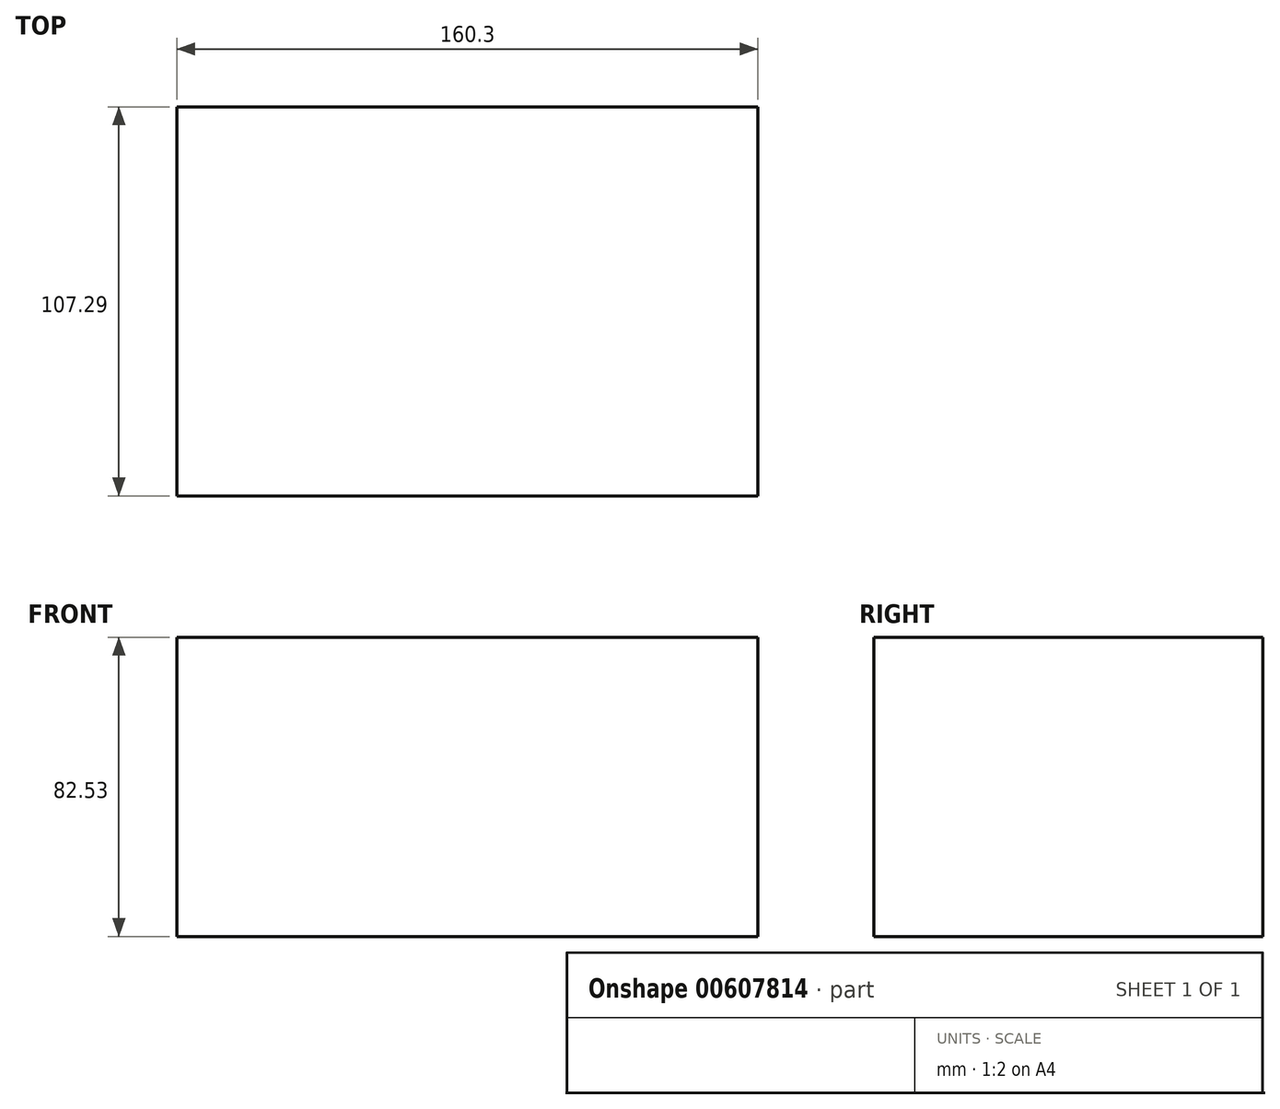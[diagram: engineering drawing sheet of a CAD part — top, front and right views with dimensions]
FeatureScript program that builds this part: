
annotation { "Feature Type Name" : "Feature", "Feature Type Description" : "" }
export const myFeature = defineFeature(function(context is Context, id is Id, definition is map)
    precondition{}
    {
        {
            var Q0;
            Q0=qCreatedBy(makeId("Top.planeOp"),FACE);
            var sketch = newSketch(context, id + "F0", { "sketchPlane" : qUnion([Q0])});
            skLineSegment(sketch, "E0.bottom", {"start": v(76.05, -45.67) * mm, "end": v(-84.25, -45.67) * mm});
            skLineSegment(sketch, "E0.top", {"start": v(76.05, 61.62) * mm, "end": v(-84.25, 61.62) * mm});
            skLineSegment(sketch, "E0.left", {"start": v(76.05, -45.67) * mm, "end": v(76.05, 61.62) * mm});
            skLineSegment(sketch, "E0.right", {"start": v(-84.25, -45.67) * mm, "end": v(-84.25, 61.62) * mm});
            skSolve(sketch);
        }
        {
            var Q0;
            Q0 = qSketchRegion(id + "F0", true);
            extrude(context, id + "F1", {"entities" : qUnion([Q0]), "depth" : 82.53 * mm, "offsetDistance" : 25.4 * mm});
        }
    });
